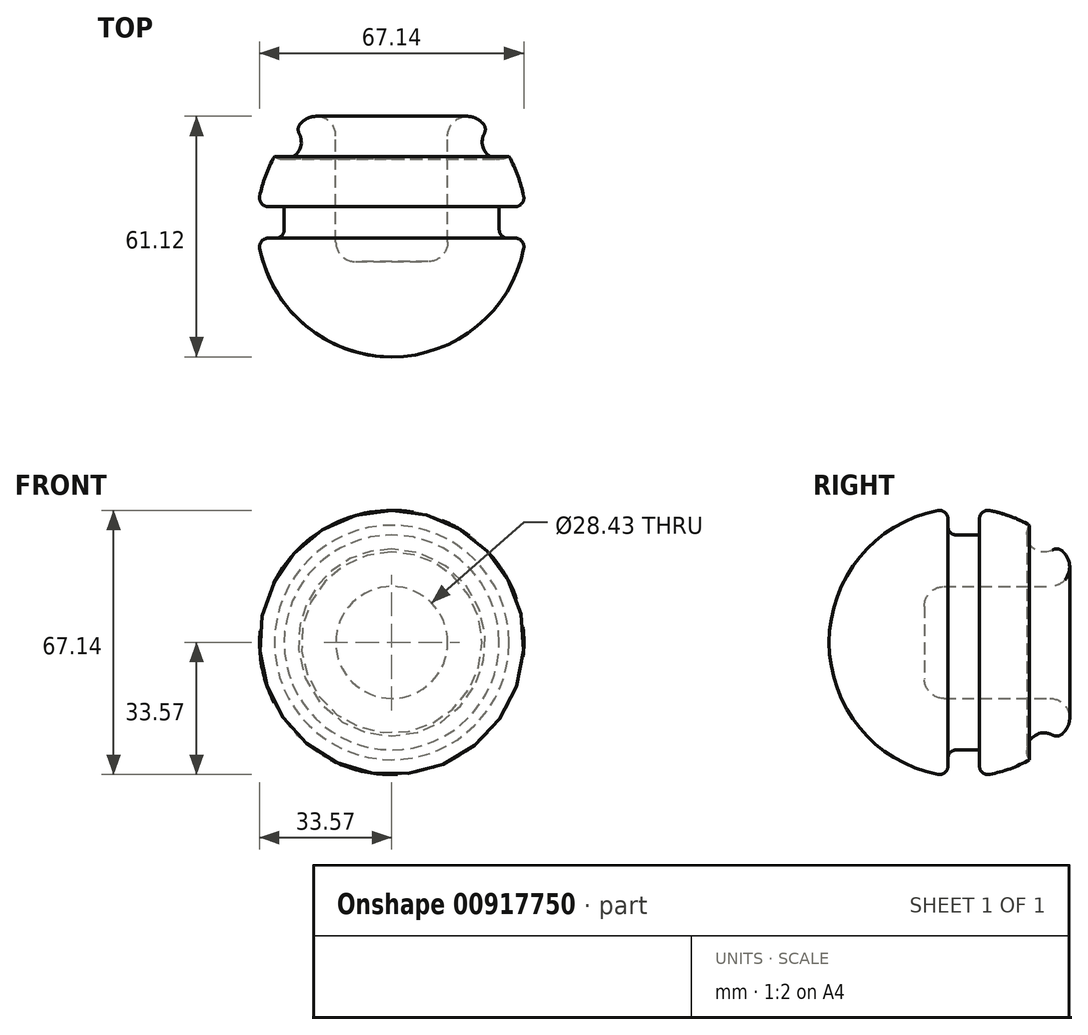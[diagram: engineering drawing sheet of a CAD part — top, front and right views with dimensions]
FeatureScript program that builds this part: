
annotation { "Feature Type Name" : "Feature", "Feature Type Description" : "" }
export const myFeature = defineFeature(function(context is Context, id is Id, definition is map)
    precondition{}
    {
        {
            var Q0;
            Q0=qCreatedBy(makeId("Top.planeOp"),FACE);
            var sketch = newSketch(context, id + "F0", { "sketchPlane" : qUnion([Q0])});
            skArc(sketch, "E0", {"start": v(-22.51, 25.7) * mm, "mid": v(-23.54, 24.77) * mm, "end": v(-24.52, 23.8) * mm});
            skLineSegment(sketch, "E1.bottom", {"start": v(0, -9.97) * mm, "end": v(-9.22, -9.97) * mm});
            skLineSegment(sketch, "E1.right", {"start": v(-14.22, -4.97) * mm, "end": v(-14.22, 21.95) * mm});
            skPoint(sketch, "E1.middle", {"position": v(0, 19.02) * mm});
            skPoint(sketch, "E1.top.end.orphan", {"position": v(-14.22, 48) * mm});
            skPoint(sketch, "E1.top.start.orphan", {"position": v(14.22, 48) * mm});
            skPoint(sketch, "E2.visualSharp", {"position": v(-14.22, -9.97) * mm});
            skArc(sketch, "E2.filletArc", {"start": v(-14.22, -4.97) * mm, "mid": v(-12.75, -8.5) * mm, "end": v(-9.22, -9.97) * mm});
            skPoint(sketch, "E3.visualSharp", {"position": v(14.22, -9.97) * mm});
            skPoint(sketch, "E4.visualSharp", {"position": v(14.22, 31.07) * mm});
            skPoint(sketch, "E5.visualSharp", {"position": v(-14.22, 31.07) * mm});
            skArc(sketch, "E5.filletArc", {"start": v(-14.22, 21.95) * mm, "mid": v(-17.15, 26.5) * mm, "end": v(-22.51, 25.7) * mm});
            skLineSegment(sketch, "E6", {"start": v(0, -9.97) * mm, "end": v(0, -34.17) * mm});
            skLineSegment(sketch, "E7.bottom", {"start": v(-27.3, -4) * mm, "end": v(-33.94, -4) * mm});
            skLineSegment(sketch, "E7.top", {"start": v(-27.3, 4) * mm, "end": v(-33.94, 4) * mm});
            skLineSegment(sketch, "E7.left", {"start": v(-27.3, -4) * mm, "end": v(-27.3, 4) * mm});
            skPoint(sketch, "E7.middle", {"position": v(-34.17, 0) * mm});
            skArc(sketch, "E8.trimOffspring", {"start": v(-33.94, -4) * mm, "mid": v(-22.7, -25.54) * mm, "end": v(0, -34.17) * mm});
            skPoint(sketch, "E7.right.end.orphan", {"position": v(-41.04, 4) * mm});
            skPoint(sketch, "E7.right.start.orphan", {"position": v(-41.04, -4) * mm});
            skPoint(sketch, "E3.filletArc.start.orphan", {"position": v(9.22, -9.97) * mm});
            skArc(sketch, "E9", {"start": v(-29.8, 16.74) * mm, "mid": v(-23.85, 17.8) * mm, "end": v(-24.52, 23.8) * mm});
            skArc(sketch, "E10.trimOffspring", {"start": v(-29.8, 16.74) * mm, "mid": v(-32.5, 10.58) * mm, "end": v(-33.94, 4) * mm});
            skSolve(sketch);
        }
        {
            var Q0;
            Q0 = qSketchRegion(id + "F0", true);
            var Q1;
            Q1=sQuery(id+"F0.wireOp",EDGE,"E6");
            revolve(context, id + "F1", {"surfaceOperationType" : NewSurfaceOperationType.NEW, "entities" : qUnion([Q0]), "axis" : qUnion([Q1]), "revolveType" : RevolveType.FULL});
        }
        {
            var Q0;
            Q0=makeQuery(id+"F1.opRevolve","SWEPT_EDGE",EDGE,{"disambiguationData":[OSD([sQuery(id+"F0.wireOp",EDGE,"E7.top"),sQuery(id+"F0.wireOp",EDGE,"E10.trimOffspring")])]});
            var Q1;
            Q1=makeQuery(id+"F1.opRevolve","SWEPT_EDGE",EDGE,{"disambiguationData":[OSD([sQuery(id+"F0.wireOp",EDGE,"E7.bottom"),sQuery(id+"F0.wireOp",EDGE,"E7.left")])]});
            var Q2;
            Q2=makeQuery(id+"F1.opRevolve","SWEPT_EDGE",EDGE,{"disambiguationData":[OSD([sQuery(id+"F0.wireOp",EDGE,"E0"),sQuery(id+"F0.wireOp",EDGE,"E9")])]});
            var Q3;
            Q3=makeQuery(id+"F1.opRevolve","SWEPT_EDGE",EDGE,{"disambiguationData":[OSD([sQuery(id+"F0.wireOp",EDGE,"E7.bottom"),sQuery(id+"F0.wireOp",EDGE,"E8.trimOffspring")])]});
            fillet(context, id + "F2", {"entities" : qUnion([Q0, Q1, Q2, Q3]), "radius" : 2.18 * mm, "tangentPropagation" : true, "allowEdgeOverflow" : false});
        }
    });
